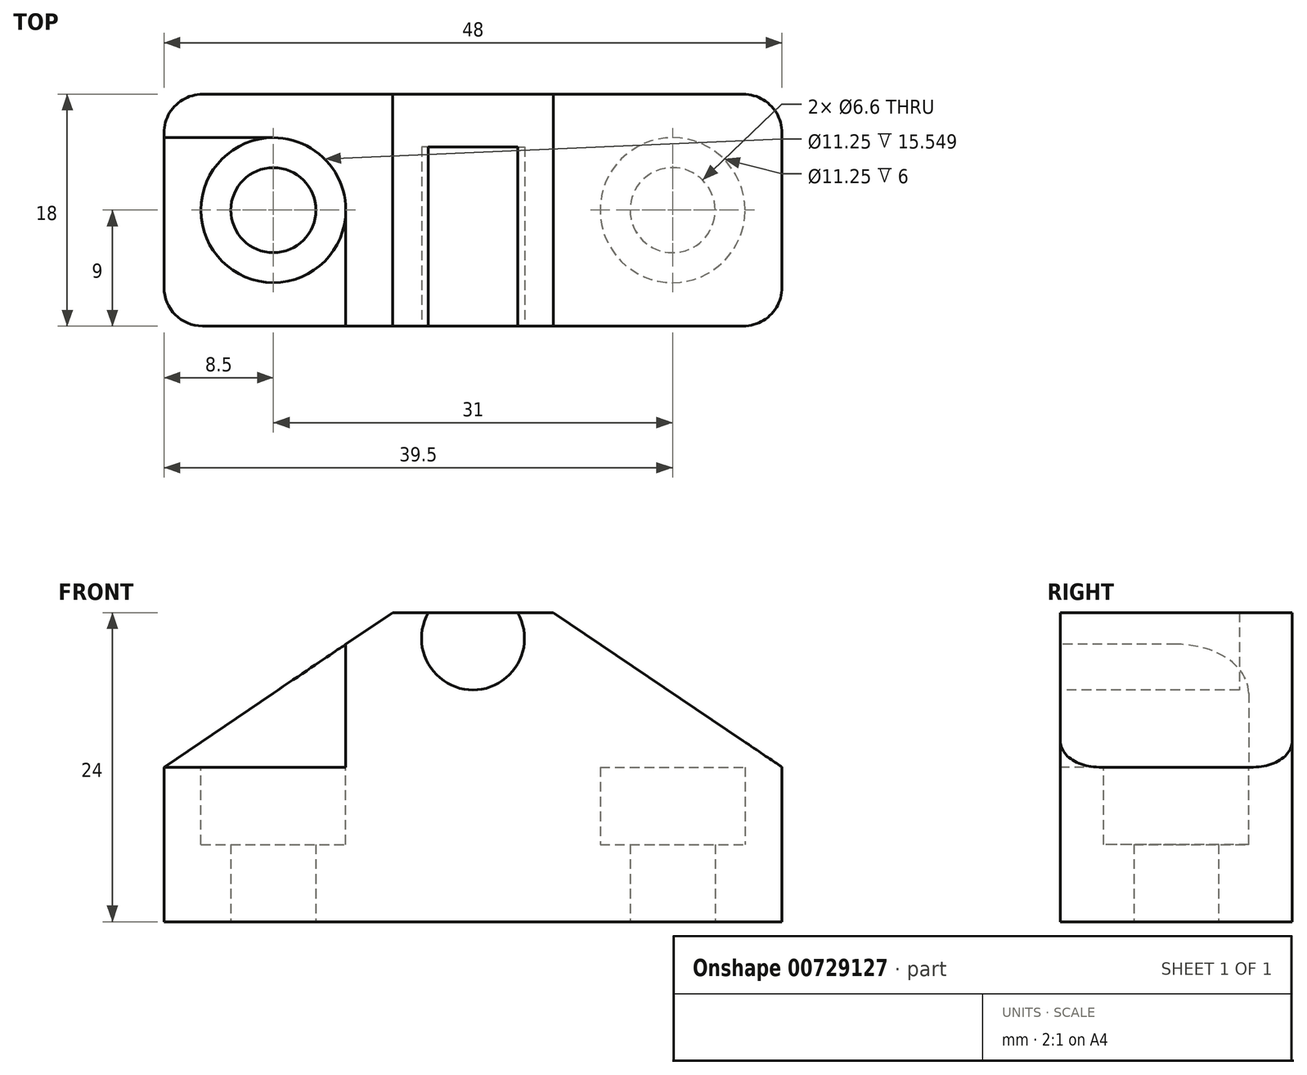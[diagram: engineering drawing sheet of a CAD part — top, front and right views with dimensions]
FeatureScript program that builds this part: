
annotation { "Feature Type Name" : "Feature", "Feature Type Description" : "" }
export const myFeature = defineFeature(function(context is Context, id is Id, definition is map)
    precondition{}
    {
        {
            var Q0;
            Q0=qCreatedBy(makeId("Front.planeOp"),FACE);
            var sketch = newSketch(context, id + "F0", { "sketchPlane" : qUnion([Q0])});
            skLineSegment(sketch, "E0", {"start": v(0, 0) * mm, "end": v(48, 0) * mm});
            skLineSegment(sketch, "E1", {"start": v(48, 0) * mm, "end": v(48, 12) * mm});
            skLineSegment(sketch, "E2", {"start": v(48, 12) * mm, "end": v(30.25, 24) * mm});
            skLineSegment(sketch, "E3", {"start": v(30.25, 24) * mm, "end": v(17.75, 24) * mm});
            skLineSegment(sketch, "E4", {"start": v(17.75, 24) * mm, "end": v(0, 12) * mm});
            skLineSegment(sketch, "E5", {"start": v(0, 12) * mm, "end": v(0, 0) * mm});
            skPoint(sketch, "E6", {"position": v(24, 24) * mm});
            skPoint(sketch, "E7", {"position": v(24, 0) * mm});
            skSolve(sketch);
        }
        {
            var Q0;
            Q0=makeQuery(id+"F0.imprint","IMPRINT",FACE,{"disambiguationData":[TD([[makeQuery(id+"F0.imprint","IMPRINT",EDGE,{"derivedFrom":sQuery(id+"F0.wireOp",EDGE,"E0")}),1.0]])]});
            extrude(context, id + "F1", {"entities" : qUnion([Q0]), "depth" : 18 * mm, "offsetDistance" : 25 * mm});
        }
        {
            var Q0;
            Q0=makeQuery(id+"F1.opExtrude","CAP_FACE",FACE,{"disambiguationData":[OSD([sQuery(id+"F0.wireOp",EDGE,"E0"),sQuery(id+"F0.wireOp",EDGE,"E1"),sQuery(id+"F0.wireOp",EDGE,"E2"),sQuery(id+"F0.wireOp",EDGE,"E3"),sQuery(id+"F0.wireOp",EDGE,"E4"),sQuery(id+"F0.wireOp",EDGE,"E5")])],"isStart":false});
            var sketch = newSketch(context, id + "F2", { "sketchPlane" : qUnion([Q0])});
            skCircle(sketch, "E8", {"center": v(24, 22) * mm, "radius": 4 * mm});
            skPoint(sketch, "E8.centerSnap0", {"position": v(24, 24) * mm});
            skPoint(sketch, "E9", {"position": v(24, 18) * mm});
            skSolve(sketch);
        }
        {
            var Q0;
            {var subQ0=sQuery(id+"F2.wireOp",EDGE,"E8");var subQ1=makeQuery(id+"F1.opExtrude","CAP_EDGE",EDGE,{"disambiguationData":[OSD([sQuery(id+"F0.wireOp",EDGE,"E3")])],"isStart":false});var subQ2=makeQuery(id+"F2.imprint","INTERSECT",VERTEX,{"disambiguationData":[OD(0.0)],"derivedFrom":[subQ1,subQ0]});Q0=makeQuery(id+"F2.imprint","IMPRINT",FACE,{"disambiguationData":[TD([[makeQuery(id+"F2.imprint","IMPRINT",EDGE,{"disambiguationData":[TD([[subQ2,1.0]])],"derivedFrom":subQ0}),1.0]])]});}
            extrude(context, id + "F3", {"entities" : qUnion([Q0]), "operationType" : NewBodyOperationType.REMOVE, "oppositeDirection" : true, "depth" : 13.9 * mm, "offsetDistance" : 25 * mm});
        }
        {
            var Q0;
            Q0=makeQuery(id+"F1.opExtrude","SWEPT_FACE",FACE,{"disambiguationData":[OSD([sQuery(id+"F0.wireOp",EDGE,"E3")])]});
            var sketch = newSketch(context, id + "F4", { "sketchPlane" : qUnion([Q0])});
            skLineSegment(sketch, "E10", {"start": v(0, -3.38) * mm, "end": v(8.5, -3.38) * mm});
            skLineSegment(sketch, "E11", {"start": v(14.12, -18) * mm, "end": v(14.12, -9) * mm});
            skLineSegment(sketch, "E12", {"start": v(0, -3.38) * mm, "end": v(0, -18) * mm});
            skLineSegment(sketch, "E13", {"start": v(0, -18) * mm, "end": v(14.12, -18) * mm});
            skArc(sketch, "E14", {"start": v(14.12, -9) * mm, "mid": v(12.48, -5.02) * mm, "end": v(8.5, -3.38) * mm});
            skLineSegment(sketch, "E15", {"start": v(24, 0) * mm, "end": v(24, -18.18) * mm, "construction": true});
            skArc(sketch, "E16.MirrorCS", {"start": v(33.88, -9) * mm, "mid": v(35.52, -5.02) * mm, "end": v(39.5, -3.38) * mm});
            skLineSegment(sketch, "E17.MirrorCS", {"start": v(48, -18) * mm, "end": v(33.88, -18) * mm});
            skLineSegment(sketch, "E18.MirrorCS", {"start": v(48, -3.37) * mm, "end": v(39.5, -3.37) * mm});
            skLineSegment(sketch, "E19.MirrorCS", {"start": v(33.88, -18) * mm, "end": v(33.88, -9) * mm});
            skLineSegment(sketch, "E20.MirrorCS", {"start": v(48, -3.37) * mm, "end": v(48, -18) * mm});
            skSolve(sketch);
        }
        {
            var Q0;
            Q0=makeQuery(id+"F4.imprint","IMPRINT",FACE,{"disambiguationData":[TD([[makeQuery(id+"F4.imprint","IMPRINT",EDGE,{"derivedFrom":sQuery(id+"F4.wireOp",EDGE,"E10")}),-1.0]])]});
            var Q1;
            Q1=makeQuery(id+"F4.imprint","IMPRINT",FACE,{"disambiguationData":[TD([[makeQuery(id+"F4.imprint","IMPRINT",EDGE,{"derivedFrom":sQuery(id+"F4.wireOp",EDGE,"E16.MirrorCS")}),-1.0]])]});
            extrude(context, id + "F5", {"entities" : qUnion([Q0, Q1]), "operationType" : NewBodyOperationType.REMOVE, "oppositeDirection" : true, "depth" : 12 * mm, "offsetDistance" : 25 * mm});
        }
        {
            var Q0;
            Q0=makeQuery(id+"F5.boolean.opBoolean","COPY",FACE,{"derivedFrom":makeQuery(id+"F5.opExtrude","CAP_FACE",FACE,{"disambiguationData":[OSD([sQuery(id+"F4.wireOp",EDGE,"E10"),sQuery(id+"F4.wireOp",EDGE,"E11"),sQuery(id+"F4.wireOp",EDGE,"E12"),sQuery(id+"F4.wireOp",EDGE,"E13"),sQuery(id+"F4.wireOp",EDGE,"E14")])],"isStart":false})});
            var sketch = newSketch(context, id + "F6", { "sketchPlane" : qUnion([Q0])});
            skPoint(sketch, "E21", {"position": v(8.5, -9) * mm});
            skPoint(sketch, "E22", {"position": v(39.5, -9) * mm});
            skSolve(sketch);
        }
        {
            var Q0;
            Q0=sQuery(id+"F6.wireOp",VERTEX,"E21");
            var Q1;
            Q1=sQuery(id+"F6.wireOp",VERTEX,"E22");
            var Q2;
            Q2=makeQuery(id+"F1.opExtrude","SWEPT_BODY",BODY,{"disambiguationData":[OSD([sQuery(id+"F0.wireOp",EDGE,"E0"),sQuery(id+"F0.wireOp",EDGE,"E1"),sQuery(id+"F0.wireOp",EDGE,"E2"),sQuery(id+"F0.wireOp",EDGE,"E3"),sQuery(id+"F0.wireOp",EDGE,"E4"),sQuery(id+"F0.wireOp",EDGE,"E5")])]});
            hole(context, id + "F7", {"style" : HoleStyle.C_BORE, "endStyle" : HoleEndStyle.THROUGH, "standardTappedOrClearance" : lookupTablePath({ "fit" : "Normal", "standard" : "ISO", "size" : "M6", "type" : "Clearance" }), "standardBlindInLast" : lookupTablePath({ "fit" : "Normal", "standard" : "ISO", "engagement" : "75%", "pitch" : "1 mm", "size" : "M6", "type" : "Clearance & tapped" }), "holeDiameter" : 6.6 * mm, "cBoreDiameter" : 11.25 * mm, "cBoreDepth" : 6 * mm, "majorDiameter" : 5 * mm, "isTappedThrough" : true, "tappedDepth" : 2.5 * mm, "tapClearance" : 3, "locations" : qUnion([Q0, Q1]), "scope" : qUnion([Q2]), "startStyle" : HoleStartStyle.PART});
        }
        {
            var Q0;
            Q0=makeQuery(id+"F1.opExtrude","CAP_EDGE",EDGE,{"disambiguationData":[OSD([sQuery(id+"F0.wireOp",EDGE,"E5")])],"isStart":true});
            var Q1;
            Q1=makeQuery(id+"F1.opExtrude","CAP_EDGE",EDGE,{"disambiguationData":[OSD([sQuery(id+"F0.wireOp",EDGE,"E5")])],"isStart":false});
            var Q2;
            Q2=makeQuery(id+"F1.opExtrude","CAP_EDGE",EDGE,{"disambiguationData":[OSD([sQuery(id+"F0.wireOp",EDGE,"E1")])],"isStart":false});
            var Q3;
            Q3=makeQuery(id+"F1.opExtrude","CAP_EDGE",EDGE,{"disambiguationData":[OSD([sQuery(id+"F0.wireOp",EDGE,"E1")])],"isStart":true});
            fillet(context, id + "F8", {"entities" : qUnion([Q0, Q1, Q2, Q3]), "radius" : 3 * mm, "tangentPropagation" : true, "allowEdgeOverflow" : false});
        }
    });
